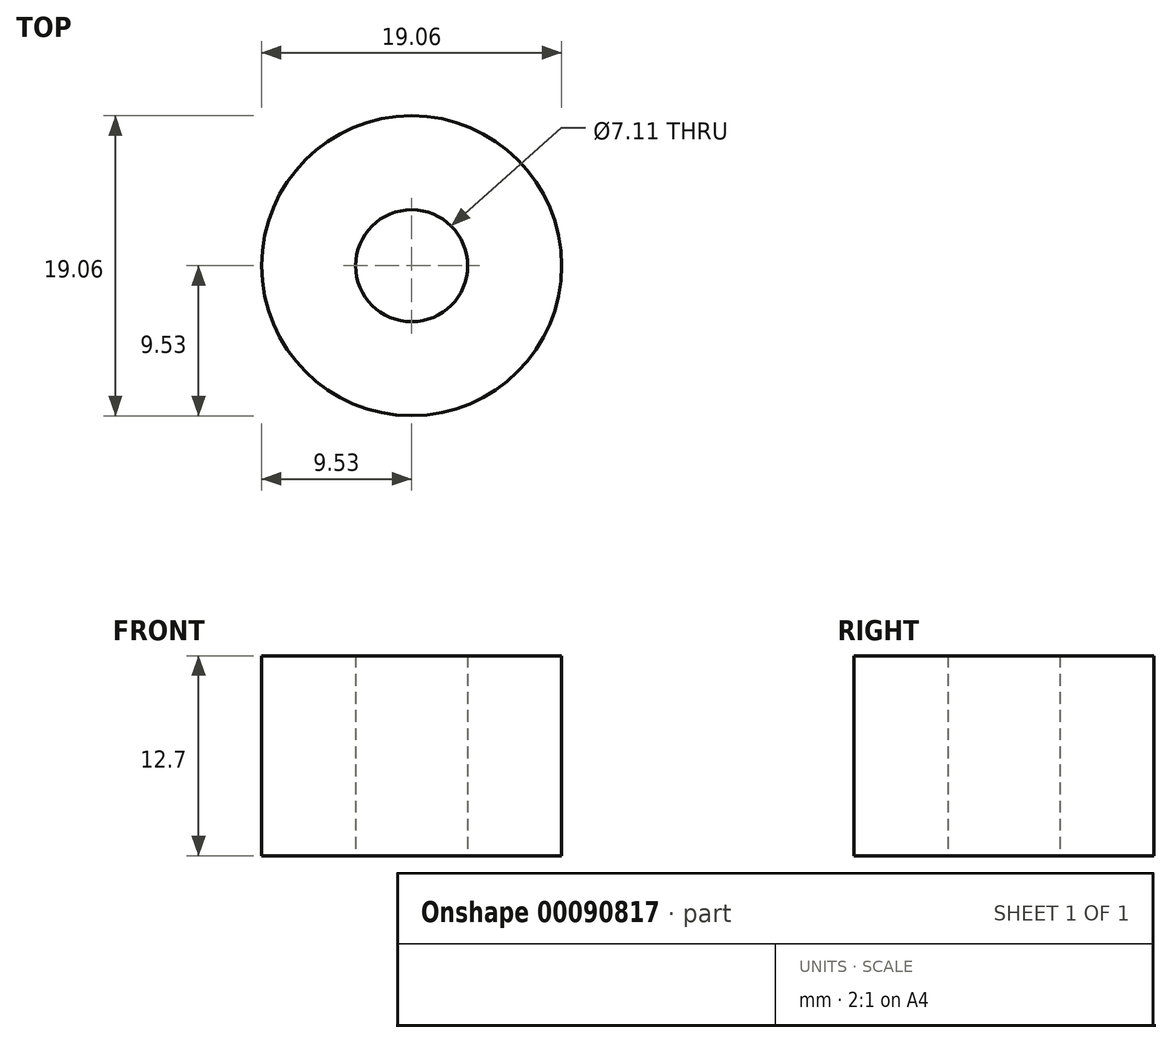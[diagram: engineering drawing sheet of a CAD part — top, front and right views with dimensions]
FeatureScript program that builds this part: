
annotation { "Feature Type Name" : "Feature", "Feature Type Description" : "" }
export const myFeature = defineFeature(function(context is Context, id is Id, definition is map)
    precondition{}
    {
        {
            var Q0;
            Q0=qCreatedBy(makeId("Top.planeOp"),FACE);
            var sketch = newSketch(context, id + "F0", { "sketchPlane" : qUnion([Q0])});
            skCircle(sketch, "E0", {"center": v(0, 0) * mm, "radius": 9.53 * mm});
            skCircle(sketch, "E1", {"center": v(0, 0) * mm, "radius": 3.56 * mm});
            skSolve(sketch);
        }
        {
            var Q0;
            Q0=makeQuery(id+"F0.imprint","IMPRINT",FACE,{"disambiguationData":[TD([[makeQuery(id+"F0.imprint","IMPRINT",EDGE,{"derivedFrom":sQuery(id+"F0.wireOp",EDGE,"E0")}),1.0]])]});
            extrude(context, id + "F1", {"entities" : qUnion([Q0]), "depth" : 12.7 * mm});
        }
    });
